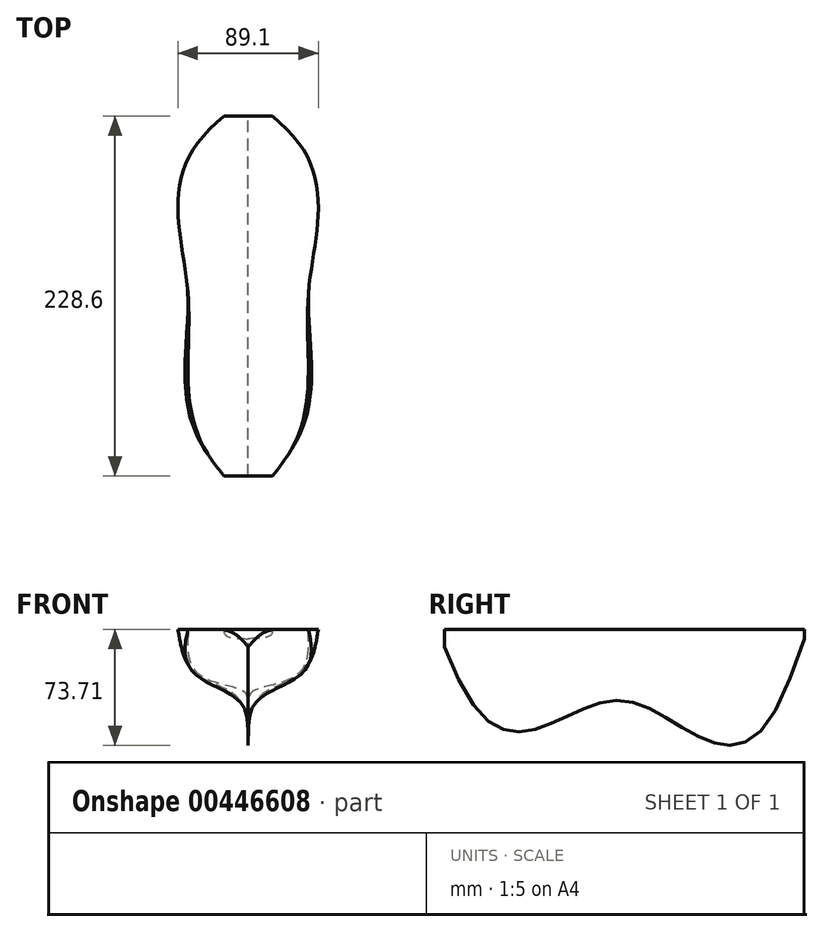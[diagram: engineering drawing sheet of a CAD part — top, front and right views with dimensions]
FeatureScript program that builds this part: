
annotation { "Feature Type Name" : "Feature", "Feature Type Description" : "" }
export const myFeature = defineFeature(function(context is Context, id is Id, definition is map)
    precondition{}
    {
        {
            var Q0;
            Q0=qCreatedBy(makeId("Top.planeOp"),FACE);
            var sketch = newSketch(context, id + "F0", { "sketchPlane" : qUnion([Q0])});
            skLineSegment(sketch, "E0", {"start": v(0, 0) * mm, "end": v(0, -254) * mm, "construction": true});
            skLineSegment(sketch, "E1", {"start": v(-38.1, -127) * mm, "end": v(38.1, -127) * mm, "construction": true});
            skSolve(sketch);
        }
        {
            var Q0;
            Q0=qCreatedBy(makeId("Front.planeOp"),FACE);
            cPlane(context, id + "F1", {"entities" : qUnion([Q0]), "cplaneType" : CPlaneType.OFFSET, "offset" : 12.7 * mm, "width" : 152.4 * mm, "height" : 152.4 * mm});
        }
        {
            var Q0;
            Q0=qCreatedBy(makeId("Front.planeOp"),FACE);
            cPlane(context, id + "F2", {"entities" : qUnion([Q0]), "cplaneType" : CPlaneType.OFFSET, "offset" : 127 * mm, "width" : 152.4 * mm, "height" : 152.4 * mm});
        }
        {
            var Q0;
            Q0=qCreatedBy(makeId("Front.planeOp"),FACE);
            cPlane(context, id + "F3", {"entities" : qUnion([Q0]), "cplaneType" : CPlaneType.OFFSET, "offset" : 241.3 * mm, "width" : 152.4 * mm, "height" : 152.4 * mm});
        }
        {
            var Q0;
            Q0=qCreatedBy(makeId("Front.planeOp"),FACE);
            cPlane(context, id + "F4", {"entities" : qUnion([Q0]), "cplaneType" : CPlaneType.OFFSET, "offset" : 25.4 * mm, "width" : 152.4 * mm, "height" : 152.4 * mm});
        }
        {
            var Q0;
            Q0=qCreatedBy(makeId("Front.planeOp"),FACE);
            cPlane(context, id + "F5", {"entities" : qUnion([Q0]), "cplaneType" : CPlaneType.OFFSET, "offset" : 228.6 * mm, "width" : 152.4 * mm, "height" : 152.4 * mm});
        }
        {
            var Q0;
            Q0=qCreatedBy(id+"F2.planeOp",FACE);
            var sketch = newSketch(context, id + "F6", { "sketchPlane" : qUnion([Q0])});
            skPoint(sketch, "E2", {"position": v(-38.1, 0) * mm});
            skPoint(sketch, "E3", {"position": v(38.1, 0) * mm});
            skFitSpline(sketch, "E4", {"points": [v(0, -45.22) * mm, v(-2.98, -39.26) * mm, v(-31.47, -28.66) * mm, v(-38.1, 0) * mm], "startDerivative": vector(-3.8, 34.13) * mm, "endDerivative": vector(2.96, 84.24) * mm});
            skFitSpline(sketch, "E5.MirrorCS", {"points": [v(0, -45.22) * mm, v(2.98, -39.26) * mm, v(31.47, -28.66) * mm, v(38.1, 0) * mm], "startDerivative": vector(3.8, 34.13) * mm, "endDerivative": vector(-2.96, 84.24) * mm});
            skLineSegment(sketch, "E6", {"start": v(-38.1, 0) * mm, "end": v(38.1, 0) * mm});
            skSolve(sketch);
        }
        {
            var Q0;
            Q0=qCreatedBy(makeId("Right.planeOp"),FACE);
            var sketch = newSketch(context, id + "F7", { "sketchPlane" : qUnion([Q0])});
            skPoint(sketch, "E7", {"position": v(-127, -45.22) * mm});
            skPoint(sketch, "E8", {"position": v(-254, 0) * mm});
            skFitSpline(sketch, "E9", {"points": [v(0, 0) * mm, v(-5.34, -2.75) * mm, v(-10.1, -5.68) * mm, v(-21.46, -38.67) * mm, v(-25.13, -41.23) * mm, v(-31.36, -42.7) * mm, v(-127, -45.22) * mm, v(-222.9, -42.59) * mm, v(-234.33, -41.86) * mm, v(-238.64, -38.76) * mm, v(-242.55, -10.91) * mm, v(-244.94, -6.51) * mm, v(-254, 0) * mm], "startDerivative": vector(-112.02, -68.16) * mm, "endDerivative": vector(-155.16, 110.05) * mm});
            skSolve(sketch);
        }
        {
            var Q0;
            Q0=qCreatedBy(id+"F5.planeOp",FACE);
            var sketch = newSketch(context, id + "F8", { "sketchPlane" : qUnion([Q0])});
            skFitSpline(sketch, "E10", {"points": [v(-24.9, 0) * mm, v(-22.34, -9) * mm, v(-6.58, -20.81) * mm, v(0, -38.74) * mm], "startDerivative": vector(1.5, -36.57) * mm, "endDerivative": vector(8.8, -53.52) * mm});
            skFitSpline(sketch, "E11.MirrorCS", {"points": [v(24.9, 0) * mm, v(22.34, -9) * mm, v(6.58, -20.81) * mm, v(0, -38.74) * mm], "startDerivative": vector(-1.5, -36.57) * mm, "endDerivative": vector(-8.8, -53.52) * mm});
            skLineSegment(sketch, "E12", {"start": v(-24.9, 0) * mm, "end": v(24.9, 0) * mm});
            skSolve(sketch);
        }
        {
            var Q0;
            Q0=qCreatedBy(id+"F4.planeOp",FACE);
            var sketch = newSketch(context, id + "F9", { "sketchPlane" : qUnion([Q0])});
            skFitSpline(sketch, "E13", {"points": [v(28.47, 0) * mm, v(23.54, -12.02) * mm, v(8.77, -20.3) * mm, v(0, -40.39) * mm], "startDerivative": vector(-8.84, -47.1) * mm, "endDerivative": vector(-15.09, -62.5) * mm});
            skFitSpline(sketch, "E14.MirrorCS", {"points": [v(-28.47, 0) * mm, v(-23.54, -12.02) * mm, v(-8.77, -20.3) * mm, v(0, -40.39) * mm], "startDerivative": vector(8.84, -47.1) * mm, "endDerivative": vector(15.09, -62.5) * mm});
            skLineSegment(sketch, "E15", {"start": v(28.47, 0) * mm, "end": v(-28.47, 0) * mm});
            skSolve(sketch);
        }
        {
            var Q0;
            Q0=qCreatedBy(id+"F1.planeOp",FACE);
            var sketch = newSketch(context, id + "F10", { "sketchPlane" : qUnion([Q0])});
            skLineSegment(sketch, "E16", {"start": v(15.4, 0) * mm, "end": v(-15.4, 0) * mm});
            skFitSpline(sketch, "E17", {"points": [v(-15.4, 0) * mm, v(-14.1, -3.94) * mm, v(0, -5.9) * mm], "startDerivative": vector(0.55, -12.69) * mm, "endDerivative": vector(27.57, -0.33) * mm});
            skFitSpline(sketch, "E18.MirrorCS", {"points": [v(15.4, 0) * mm, v(14.1, -3.94) * mm, v(0, -5.9) * mm], "startDerivative": vector(-0.55, -12.69) * mm, "endDerivative": vector(-27.57, -0.33) * mm});
            skSolve(sketch);
        }
        {
            var Q0;
            Q0=qCreatedBy(id+"F3.planeOp",FACE);
            var sketch = newSketch(context, id + "F11", { "sketchPlane" : qUnion([Q0])});
            skPoint(sketch, "E19", {"position": v(-15.4, 0) * mm});
            skPoint(sketch, "E20", {"position": v(15.4, 0) * mm});
            skFitSpline(sketch, "E21", {"points": [v(-15.4, 0) * mm, v(-7.58, -3.47) * mm, v(0, -11.2) * mm], "startDerivative": vector(17.18, -5.66) * mm, "endDerivative": vector(13.7, -16.52) * mm});
            skFitSpline(sketch, "E22.MirrorCS", {"points": [v(15.4, 0) * mm, v(7.58, -3.47) * mm, v(0, -11.2) * mm], "startDerivative": vector(-17.18, -5.66) * mm, "endDerivative": vector(-13.7, -16.52) * mm});
            skLineSegment(sketch, "E23", {"start": v(-15.4, 0) * mm, "end": v(15.4, 0) * mm});
            skSolve(sketch);
        }
        {
            var Q0;
            Q0=makeQuery(id+"F11.imprint","IMPRINT",FACE,{"disambiguationData":[TD([[makeQuery(id+"F11.imprint","IMPRINT",EDGE,{"derivedFrom":sQuery(id+"F11.wireOp",EDGE,"E21")}),1.0]])]});
            var Q1;
            Q1=makeQuery(id+"F8.imprint","IMPRINT",FACE,{"disambiguationData":[TD([[makeQuery(id+"F8.imprint","IMPRINT",EDGE,{"derivedFrom":sQuery(id+"F8.wireOp",EDGE,"E10")}),1.0]])]});
            var Q2;
            Q2=makeQuery(id+"F6.imprint","IMPRINT",FACE,{"disambiguationData":[TD([[makeQuery(id+"F6.imprint","IMPRINT",EDGE,{"derivedFrom":sQuery(id+"F6.wireOp",EDGE,"E4")}),-1.0]])]});
            var Q3;
            Q3=makeQuery(id+"F9.imprint","IMPRINT",FACE,{"disambiguationData":[TD([[makeQuery(id+"F9.imprint","IMPRINT",EDGE,{"derivedFrom":sQuery(id+"F9.wireOp",EDGE,"E13")}),-1.0]])]});
            var Q4;
            Q4=makeQuery(id+"F10.imprint","IMPRINT",FACE,{"disambiguationData":[TD([[makeQuery(id+"F10.imprint","IMPRINT",EDGE,{"derivedFrom":sQuery(id+"F10.wireOp",EDGE,"E16")}),1.0]])]});
            loft(context, id + "F12", {"sheetProfilesArray" : [{ "sheetProfileEntities" : qUnion([Q0]) }, { "sheetProfileEntities" : qUnion([Q1]) }, { "sheetProfileEntities" : qUnion([Q2]) }, { "sheetProfileEntities" : qUnion([Q3]) }, { "sheetProfileEntities" : qUnion([Q4]) }]});
        }
    });
